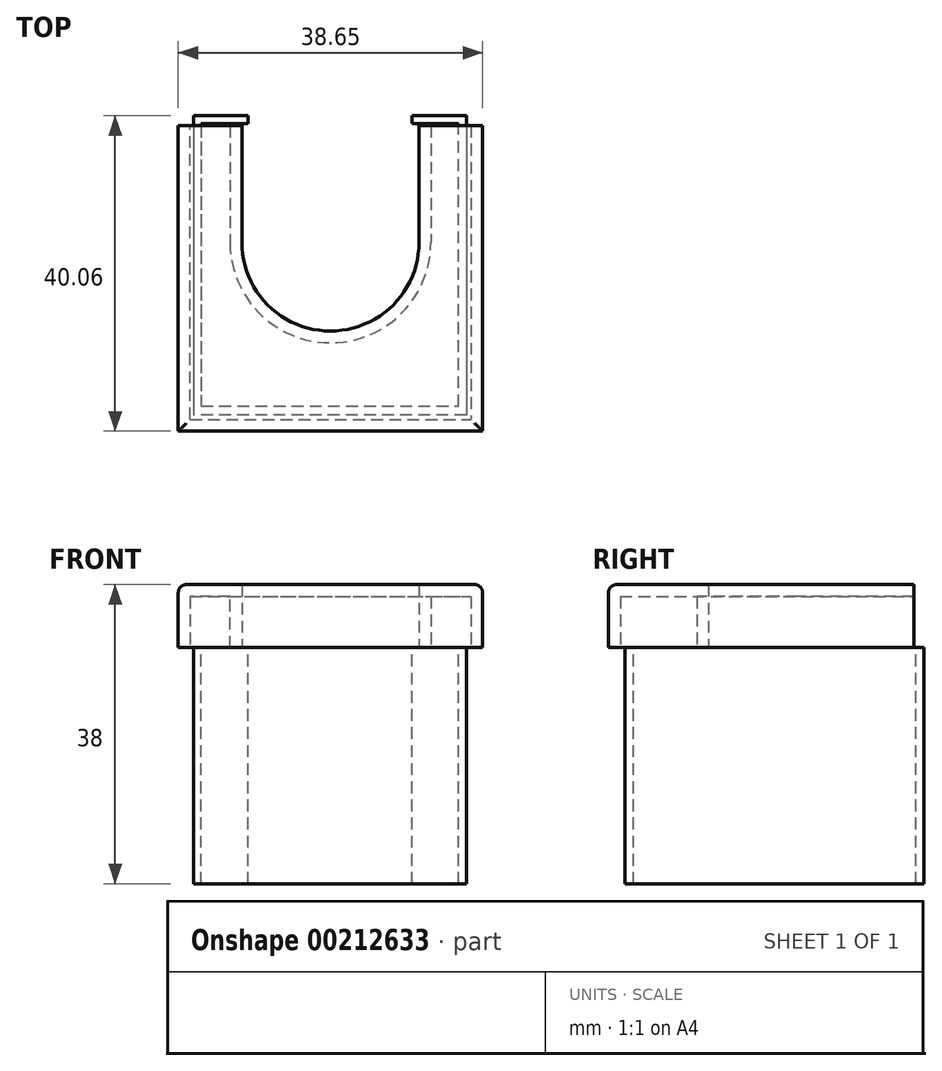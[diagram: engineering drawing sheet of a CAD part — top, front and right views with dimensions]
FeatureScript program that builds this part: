
annotation { "Feature Type Name" : "Feature", "Feature Type Description" : "" }
export const myFeature = defineFeature(function(context is Context, id is Id, definition is map)
    precondition{}
    {
        {
            var Q0;
            Q0=qCreatedBy(makeId("Top.planeOp"),FACE);
            var sketch = newSketch(context, id + "F0", { "sketchPlane" : qUnion([Q0])});
            skLineSegment(sketch, "E0", {"start": v(-17.36, 14.36) * mm, "end": v(-10.46, 14.36) * mm});
            skLineSegment(sketch, "E1", {"start": v(-10.46, 14.36) * mm, "end": v(-10.46, 13.36) * mm});
            skLineSegment(sketch, "E2", {"start": v(-10.46, 13.36) * mm, "end": v(-16.4, 13.36) * mm});
            skLineSegment(sketch, "E3", {"start": v(-16.4, 13.36) * mm, "end": v(-16.4, -22.64) * mm});
            skLineSegment(sketch, "E4", {"start": v(-16.4, -22.54) * mm, "end": v(16.29, -22.54) * mm});
            skLineSegment(sketch, "E5", {"start": v(16.29, -22.64) * mm, "end": v(16.29, 13.36) * mm});
            skLineSegment(sketch, "E6", {"start": v(16.29, 13.36) * mm, "end": v(10.39, 13.36) * mm});
            skLineSegment(sketch, "E7", {"start": v(10.39, 13.36) * mm, "end": v(10.39, 14.36) * mm});
            skLineSegment(sketch, "E8", {"start": v(10.39, 14.36) * mm, "end": v(17.29, 14.36) * mm});
            skLineSegment(sketch, "E9", {"start": v(17.29, 14.36) * mm, "end": v(17.29, -23.64) * mm});
            skLineSegment(sketch, "E10", {"start": v(17.29, -23.64) * mm, "end": v(-17.36, -23.64) * mm});
            skLineSegment(sketch, "E11", {"start": v(-17.36, 14.36) * mm, "end": v(-17.36, -23.64) * mm});
            skPoint(sketch, "E12", {"position": v(0, -4.64) * mm});
            skLineSegment(sketch, "E13", {"start": v(-16.4, -22.54) * mm, "end": v(16.29, 13.36) * mm, "construction": true});
            skLineSegment(sketch, "E14", {"start": v(16.29, -22.54) * mm, "end": v(-16.4, 13.36) * mm, "construction": true});
            skPoint(sketch, "E15", {"position": v(-0.06, -4.59) * mm});
            skSolve(sketch);
        }
        {
            var Q0;
            Q0=qCreatedBy(makeId("Top.planeOp"),FACE);
            var sketch = newSketch(context, id + "F1", { "sketchPlane" : qUnion([Q0])});
            skLineSegment(sketch, "E16", {"start": v(-19.3, -25.7) * mm, "end": v(19.35, -25.7) * mm});
            skLineSegment(sketch, "E17", {"start": v(-19.3, -25.7) * mm, "end": v(-19.3, 15.5) * mm});
            skLineSegment(sketch, "E18", {"start": v(19.35, 15.5) * mm, "end": v(19.35, -25.7) * mm});
            skLineSegment(sketch, "E19", {"start": v(-19.3, 15.5) * mm, "end": v(-11.23, 15.5) * mm});
            skLineSegment(sketch, "E20", {"start": v(19.35, 15.5) * mm, "end": v(11.27, 15.5) * mm});
            skArc(sketch, "E21", {"start": v(-11.23, -1.7) * mm, "mid": v(0.02, -12.98) * mm, "end": v(11.27, -1.7) * mm});
            skLineSegment(sketch, "E22", {"start": v(-11.23, 15.5) * mm, "end": v(-11.23, -1.7) * mm});
            skLineSegment(sketch, "E23", {"start": v(11.27, 15.5) * mm, "end": v(11.27, -1.7) * mm});
            skSolve(sketch);
        }
        {
            var Q0;
            Q0=makeQuery(id+"F1.imprint","IMPRINT",FACE,{"disambiguationData":[TD([[makeQuery(id+"F1.imprint","IMPRINT",EDGE,{"derivedFrom":sQuery(id+"F1.wireOp",EDGE,"E16")}),1.0]])]});
            extrude(context, id + "F2", {"entities" : qUnion([Q0]), "depth" : 8 * mm});
        }
        {
            var Q0;
            Q0=makeQuery(id+"F2.opExtrude","CAP_FACE",FACE,{"disambiguationData":[OSD([sQuery(id+"F1.wireOp",EDGE,"E16"),sQuery(id+"F1.wireOp",EDGE,"Tlbrq81f-UYma-3GCr-Liw0-ozQQkh8nIJft"),sQuery(id+"F1.wireOp",EDGE,"H1VRcAHF-lP1v-FzLu-LK0t-7K9fiYyhv24Q"),sQuery(id+"F1.wireOp",EDGE,"LF9LERii-Tz4R-MFiL-iWUK-0L1QVpkCMieU"),sQuery(id+"F1.wireOp",EDGE,"dF1Gm0Rx-ivYt-yQ3h-9dWT-o0EyTlRdCvNU"),sQuery(id+"F1.wireOp",EDGE,"7gwea0EE-G0O7-2qTG-MZvY-VAdS4jyp05UZ"),sQuery(id+"F1.wireOp",EDGE,"cgyyApHP-Rveb-rplj-wEBS-NCvlhXazGAQ3"),sQuery(id+"F1.wireOp",EDGE,"HRl3Ql93-RCh9-pMvM-FS4K-rGivZDXxRngf")])],"isStart":true});
            shell(context, id + "F3", {"entities" : qUnion([Q0]), "thickness" : 1.5 * mm});
        }
        {
            var Q0;
            Q0=makeQuery(id+"F2.opExtrude","SWEPT_FACE",FACE,{"disambiguationData":[OSD([sQuery(id+"F1.wireOp",EDGE,"LF9LERii-Tz4R-MFiL-iWUK-0L1QVpkCMieU")])]});
            var Q1;
            Q1=makeQuery(id+"F2.opExtrude","SWEPT_FACE",FACE,{"disambiguationData":[OSD([sQuery(id+"F1.wireOp",EDGE,"dF1Gm0Rx-ivYt-yQ3h-9dWT-o0EyTlRdCvNU")])]});
            var Q2;
            Q2=makeQuery(id+"F2.opExtrude","SWEPT_FACE",FACE,{"disambiguationData":[OSD([sQuery(id+"F1.wireOp",EDGE,"E20")])]});
            var Q3;
            Q3=makeQuery(id+"F2.opExtrude","SWEPT_FACE",FACE,{"disambiguationData":[OSD([sQuery(id+"F1.wireOp",EDGE,"E19")])]});
            extrude(context, id + "F4", {"entities" : qUnion([Q0, Q1, Q2, Q3]), "operationType" : NewBodyOperationType.REMOVE, "oppositeDirection" : true, "depth" : 2.4 * mm});
        }
        {
            var Q0;
            Q0=makeQuery(id+"F2.opExtrude","CAP_EDGE",EDGE,{"disambiguationData":[OSD([sQuery(id+"F1.wireOp",EDGE,"E17")])],"isStart":false});
            var Q1;
            Q1=makeQuery(id+"F2.opExtrude","CAP_EDGE",EDGE,{"disambiguationData":[OSD([sQuery(id+"F1.wireOp",EDGE,"g3S2oytQ-AaI5-DDn9-ciXv-o9xc1VYy2N9o")])],"isStart":false});
            var Q2;
            Q2=makeQuery(id+"F2.opExtrude","CAP_EDGE",EDGE,{"disambiguationData":[OSD([sQuery(id+"F1.wireOp",EDGE,"7gwea0EE-G0O7-2qTG-MZvY-VAdS4jyp05UZ")])],"isStart":false});
            var Q3;
            Q3=makeQuery(id+"F2.opExtrude","CAP_EDGE",EDGE,{"disambiguationData":[OSD([sQuery(id+"F1.wireOp",EDGE,"tIOeHqpV-oqyI-kJBn-Z8kw-mpTQ9swV2XpE")])],"isStart":false});
            var Q4;
            Q4=makeQuery(id+"F2.opExtrude","CAP_EDGE",EDGE,{"disambiguationData":[OSD([sQuery(id+"F1.wireOp",EDGE,"E18")])],"isStart":false});
            var Q5;
            Q5=makeQuery(id+"F2.opExtrude","CAP_EDGE",EDGE,{"disambiguationData":[OSD([sQuery(id+"F1.wireOp",EDGE,"E16")])],"isStart":false});
            fillet(context, id + "F5", {"entities" : qUnion([Q0, Q1, Q2, Q3, Q4, Q5]), "radius" : 1 * mm, "tangentPropagation" : true, "allowEdgeOverflow" : false});
        }
        {
            var Q0;
            {var subQ1=sQuery(id+"F0.wireOp",EDGE,"E0");Q0=makeQuery(id+"F0.imprint","IMPRINT",FACE,{"disambiguationData":[TD([[makeQuery(id+"F0.imprint","IMPRINT",EDGE,{"derivedFrom":subQ1}),-1.0]])]});}
            extrude(context, id + "F6", {"entities" : qUnion([Q0]), "oppositeDirection" : true, "depth" : 30 * mm});
        }
    });
